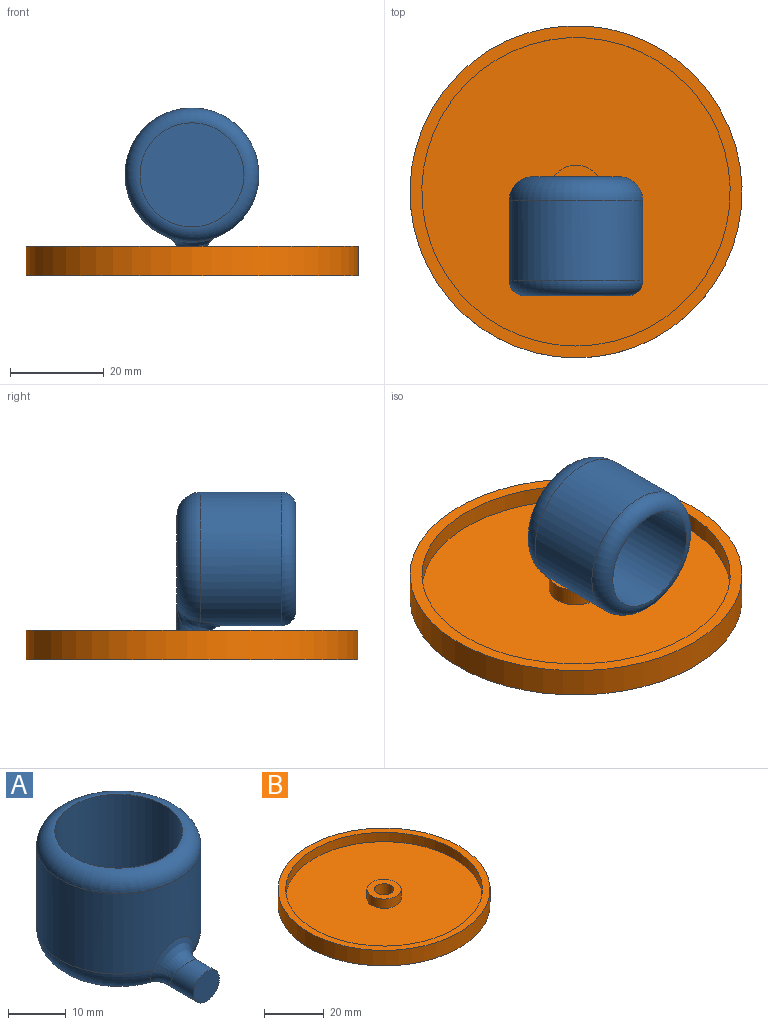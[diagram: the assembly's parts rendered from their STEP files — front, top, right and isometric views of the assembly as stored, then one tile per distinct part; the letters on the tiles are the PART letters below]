
ASSEMBLY  parts=2 mates=1
PART A: 11 faces, bbox 30.9x37.1x25.4 mm
  f0: cylinder r=14.29mm len=28.58mm, axis (0,0,-1), area 1506.3mm2, adj f6,f8,f10
  f1: plane 18.42x18.42mm, normal (0,0,-1), area 266.3mm2, adj f6
  f2: cylinder r=3.17mm len=12.38mm, axis (0,1,0), area 129.4mm2, adj f3,f7,f8,f9
  f3: plane 6.35x6.35mm, normal (0,-1,0), area 31.7mm2, adj f2
  f4: cylinder r=11.11mm len=22.23mm, axis (0,0,1), area 1330.1mm2, adj f5,f10
  f5: plane 22.23x22.23mm, normal (0,0,1), area 387.9mm2, adj f4
  f6: torus R=9.21mm, axis (0,0,1), area 564.2mm2, adj f0,f1,f7,f9
  f7: bspline ~7.27x5.85mm, area 20.5mm2, adj f2,f6,f8
  f8: bspline ~10.36x6.06mm, area 46.3mm2, adj f0,f2,f7,f9
  f9: bspline ~7.27x5.85mm, area 20.5mm2, adj f2,f6,f8
  f10: torus R=11.11mm, axis (0,0,1), area 411.6mm2, adj f0,f4
PART B: 8 faces, bbox 70.9x70.9x6.4 mm
  f0: plane 11.43x11.43mm, normal (0,0,1), area 70.9mm2, adj f4,f7
  f1: cylinder r=35.47mm len=70.94mm, axis (0,0,-1), area 1415.1mm2, adj f2,f3
  f2: plane 70.94x70.94mm, normal (0,0,1), area 545.8mm2, adj f1,f5
  f3: plane 70.94x70.94mm, normal (0,0,-1), area 3920.5mm2, adj f1,f4
  f4: cylinder r=3.17mm len=6.35mm, axis (0,0,-1), area 126.7mm2, adj f0,f3
  f5: cylinder r=32.93mm len=65.86mm, axis (0,0,-1), area 788.3mm2, adj f2,f6
  f6: plane 65.86x65.86mm, normal (0,0,1), area 3303.8mm2, adj f5,f7
  f7: cylinder r=5.71mm len=11.43mm, axis (0,0,-1), area 136.8mm2, adj f0,f6
PLACE A rot(axis=(1,0,0),90deg) t=(10.07,0.55,21.59)mm fixed
PLACE B rot(axis=(0,0,1),93.5deg) t=(10.07,-2.62,0)mm
MATE revolute A.f2 <-> B.f1  axis (0,0,-1) through (10.07,-2.62,0)mm
